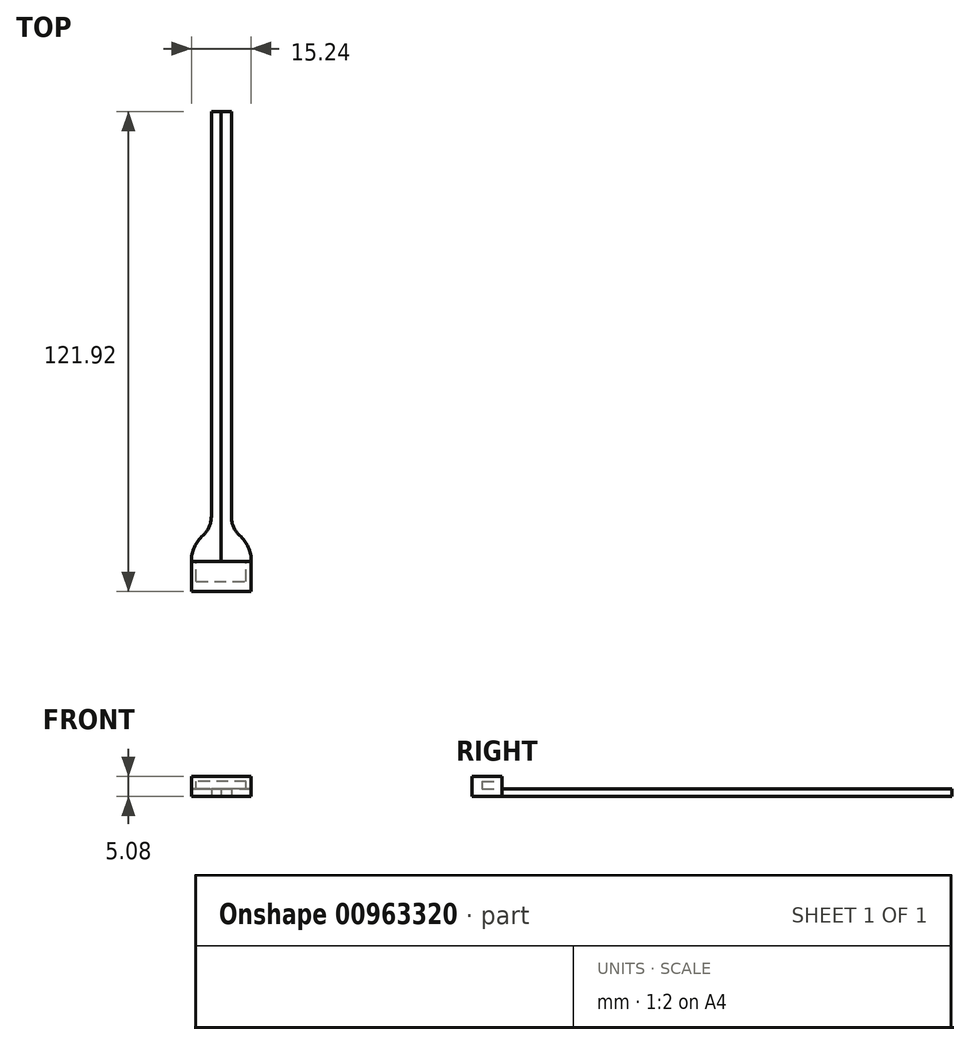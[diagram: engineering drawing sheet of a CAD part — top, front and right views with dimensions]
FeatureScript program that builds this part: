
annotation { "Feature Type Name" : "Feature", "Feature Type Description" : "" }
export const myFeature = defineFeature(function(context is Context, id is Id, definition is map)
    precondition{}
    {
        {
            var Q0;
            Q0=qCreatedBy(makeId("Top.planeOp"),FACE);
            var sketch = newSketch(context, id + "F0", { "sketchPlane" : qUnion([Q0])});
            skLineSegment(sketch, "E0.bottom", {"start": v(0, 0) * mm, "end": v(15.24, 0) * mm});
            skLineSegment(sketch, "E0.top", {"start": v(0, 7.62) * mm, "end": v(15.24, 7.62) * mm});
            skLineSegment(sketch, "E0.left", {"start": v(0, 0) * mm, "end": v(0, 7.62) * mm});
            skLineSegment(sketch, "E0.right", {"start": v(15.24, 0) * mm, "end": v(15.24, 7.62) * mm});
            skSolve(sketch);
        }
        {
            var Q0;
            Q0=makeQuery(id+"F0.imprint","IMPRINT",FACE,{"disambiguationData":[TD([[makeQuery(id+"F0.imprint","IMPRINT",EDGE,{"derivedFrom":sQuery(id+"F0.wireOp",EDGE,"E0.bottom")}),1.0]])]});
            var Q1;
            {var subQ0=sQuery(id+"F0.wireOp",EDGE,"zsi7gBfR-j4X2-UrOj-o1LC-GleYWkfHhouP");Q1=makeQuery(id+"F0.imprint","IMPRINT",FACE,{"disambiguationData":[TD([[makeQuery(id+"F0.imprint","IMPRINT",EDGE,{"derivedFrom":subQ0}),-1.0]])]});}
            extrude(context, id + "F1", {"entities" : qUnion([Q0, Q1]), "depth" : 5.08 * mm, "offsetDistance" : 25.4 * mm});
        }
        {
            var Q0;
            Q0=makeQuery(id+"F1.opExtrude","SWEPT_FACE",FACE,{"disambiguationData":[OSD([sQuery(id+"F0.wireOp",EDGE,"E0.top")])]});
            var sketch = newSketch(context, id + "F2", { "sketchPlane" : qUnion([Q0])});
            skLineSegment(sketch, "E1.bottom", {"start": v(-13.97, 1.9) * mm, "end": v(-1.27, 1.9) * mm});
            skLineSegment(sketch, "E1.top", {"start": v(-13.97, 3.81) * mm, "end": v(-1.27, 3.81) * mm});
            skLineSegment(sketch, "E1.left", {"start": v(-13.97, 1.9) * mm, "end": v(-13.97, 3.81) * mm});
            skLineSegment(sketch, "E1.right", {"start": v(-1.27, 1.9) * mm, "end": v(-1.27, 3.81) * mm});
            skSolve(sketch);
        }
        {
            var Q0;
            Q0=makeQuery(id+"F2.imprint","IMPRINT",FACE,{"disambiguationData":[TD([[makeQuery(id+"F2.imprint","IMPRINT",EDGE,{"derivedFrom":sQuery(id+"F2.wireOp",EDGE,"E1.bottom")}),1.0]])]});
            extrude(context, id + "F3", {"entities" : qUnion([Q0]), "operationType" : NewBodyOperationType.REMOVE, "endBound" : BoundingType.UP_TO_NEXT, "oppositeDirection" : true, "depth" : 9.14 * mm, "hasOffset" : true, "offsetDistance" : 2.54 * mm});
        }
        {
            var Q0;
            Q0=makeQuery(id+"F1.opExtrude","CAP_FACE",FACE,{"disambiguationData":[OSD([sQuery(id+"F0.wireOp",EDGE,"E0.bottom"),sQuery(id+"F0.wireOp",EDGE,"E0.top"),sQuery(id+"F0.wireOp",EDGE,"E0.left"),sQuery(id+"F0.wireOp",EDGE,"E0.right")])],"isStart":true});
            var sketch = newSketch(context, id + "F4", { "sketchPlane" : qUnion([Q0])});
            skArc(sketch, "E2", {"start": v(12.28, -14.25) * mm, "mid": v(14.47, -11.25) * mm, "end": v(15.24, -7.62) * mm});
            skArc(sketch, "E3", {"start": v(12.28, -14.25) * mm, "mid": v(10.71, -16.39) * mm, "end": v(10.16, -18.98) * mm});
            skLineSegment(sketch, "E4", {"start": v(10.16, -18.98) * mm, "end": v(10.16, -121.92) * mm});
            skLineSegment(sketch, "E5", {"start": v(7.62, 0) * mm, "end": v(7.62, -45.64) * mm, "construction": true});
            skLineSegment(sketch, "E6", {"start": v(10.16, -121.92) * mm, "end": v(7.62, -121.92) * mm});
            skLineSegment(sketch, "E7", {"start": v(7.62, -121.92) * mm, "end": v(7.62, -7.62) * mm});
            skLineSegment(sketch, "E8", {"start": v(7.62, -7.62) * mm, "end": v(15.24, -7.62) * mm});
            skSolve(sketch);
        }
        {
            var Q0;
            Q0=makeQuery(id+"F4.imprint","IMPRINT",FACE,{"disambiguationData":[TD([[makeQuery(id+"F4.imprint","IMPRINT",EDGE,{"derivedFrom":sQuery(id+"F4.wireOp",EDGE,"E2")}),1.0]])]});
            var Q1;
            Q1=makeQuery(id+"F3.boolean.opBoolean","COPY",FACE,{"derivedFrom":makeQuery(id+"F3.opExtrude","SWEPT_FACE",FACE,{"disambiguationData":[OSD([sQuery(id+"F2.wireOp",EDGE,"E1.bottom")])]})});
            extrude(context, id + "F5", {"entities" : qUnion([Q0]), "endBound" : BoundingType.UP_TO_SURFACE, "oppositeDirection" : true, "depth" : 25.4 * mm, "endBoundEntityFace" : qUnion([Q1]), "offsetDistance" : 25.4 * mm});
        }
        {
            var Q0;
            Q0=makeQuery(id+"F5.opExtrude","SWEPT_BODY",BODY,{"disambiguationData":[OSD([sQuery(id+"F4.wireOp",EDGE,"E2"),sQuery(id+"F4.wireOp",EDGE,"E3"),sQuery(id+"F4.wireOp",EDGE,"E4"),sQuery(id+"F4.wireOp",EDGE,"E6"),sQuery(id+"F4.wireOp",EDGE,"E7"),sQuery(id+"F4.wireOp",EDGE,"E8")])]});
            var Q1;
            Q1=makeQuery(id+"F5.opExtrude","SWEPT_FACE",FACE,{"disambiguationData":[OSD([sQuery(id+"F4.wireOp",EDGE,"E7")])]});
            mirror(context, id + "F6", {"entities" : qUnion([Q0]), "mirrorPlane" : qUnion([Q1])});
        }
    });
